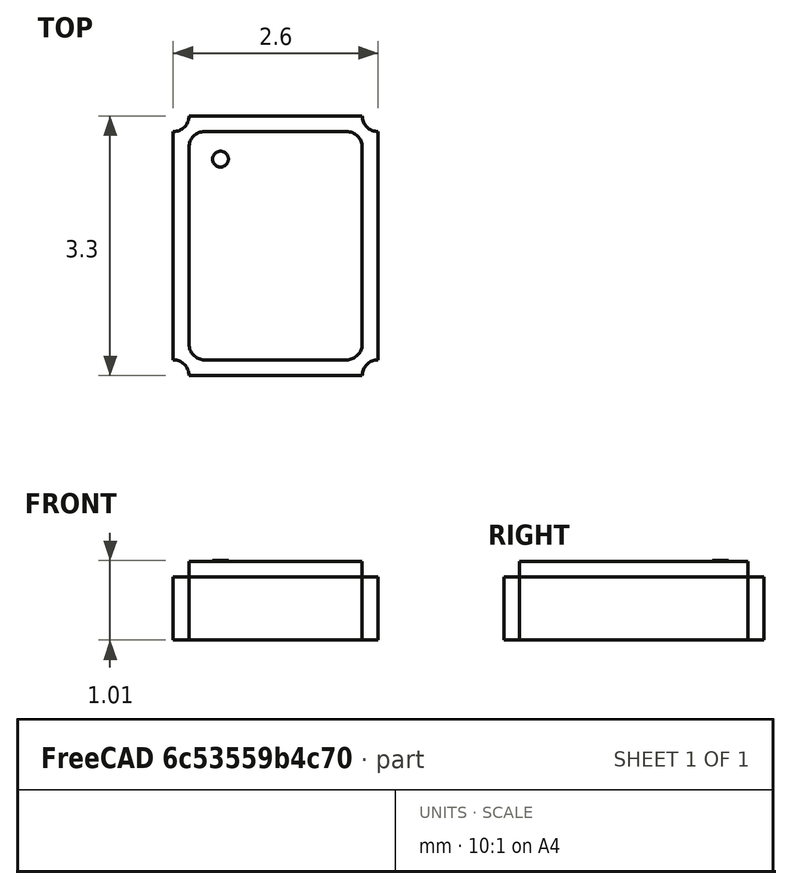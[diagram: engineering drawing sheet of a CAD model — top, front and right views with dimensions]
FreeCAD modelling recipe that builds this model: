
FCSTD DOCUMENT
Label: OSCCC250X320X100_4
objects: Part::Cylinder×5, Part::Box×2, Part::MultiFuse×2, Part::Cut×1, Part::Fillet×1
note: 11 computed .brp shape members not serialized (recipe doc carries the construction recipe); baked Part::Feature solids carry a one-line shape summary decoded from their .brp

FEATURE [Part::Box] Box
  Height = 0.8
  Length = 2.6
  Placement = pos=(-1.3,-1.65,0) rot=(0,0,1;0rad)
  Width = 3.3
FEATURE [Part::Cylinder] Cylinder
  Angle = 360
  Height = 3
  Placement = pos=(-1.3,-1.65,-1) rot=(0,0,1;0rad)
  Radius = 0.2
FEATURE [Part::Cylinder] Cylinder001
  Angle = 360
  Height = 3
  Placement = pos=(1.3,-1.65,-1) rot=(0,0,1;0rad)
  Radius = 0.2
FEATURE [Part::Cylinder] Cylinder002
  Angle = 360
  Height = 3
  Placement = pos=(-1.3,1.65,-1) rot=(0,0,1;0rad)
  Radius = 0.2
FEATURE [Part::Cylinder] Cylinder003
  Angle = 360
  Height = 3
  Placement = pos=(1.3,1.65,-1) rot=(0,0,1;0rad)
  Radius = 0.2
FEATURE [Part::MultiFuse] Fusion
  Shapes = -> [Cylinder,Cylinder001,Cylinder002,Cylinder003]
FEATURE [Part::Cut] Cut
  Base = -> Box
  Tool = -> Fusion
FEATURE [Part::Box] Box001
  Height = 0.2
  Length = 2.2
  Placement = pos=(-1.1,-1.45,0.8) rot=(0,0,1;0rad)
  Width = 2.9
FEATURE [Part::Fillet] Fillet
  Base = -> Box001
  Edges = 4 edges r=0.2: [Edge1,Edge3,Edge5,Edge7]
FEATURE [Part::Cylinder] Cylinder004
  Angle = 360
  Height = 0.01
  Placement = pos=(-0.7,1.1,1) rot=(0,0,1;0rad)
  Radius = 0.1
FEATURE [Part::MultiFuse] Fusion001  label="OSCCC250X320X100_4"
  Shapes = -> [Cut,Fillet,Cylinder004]
